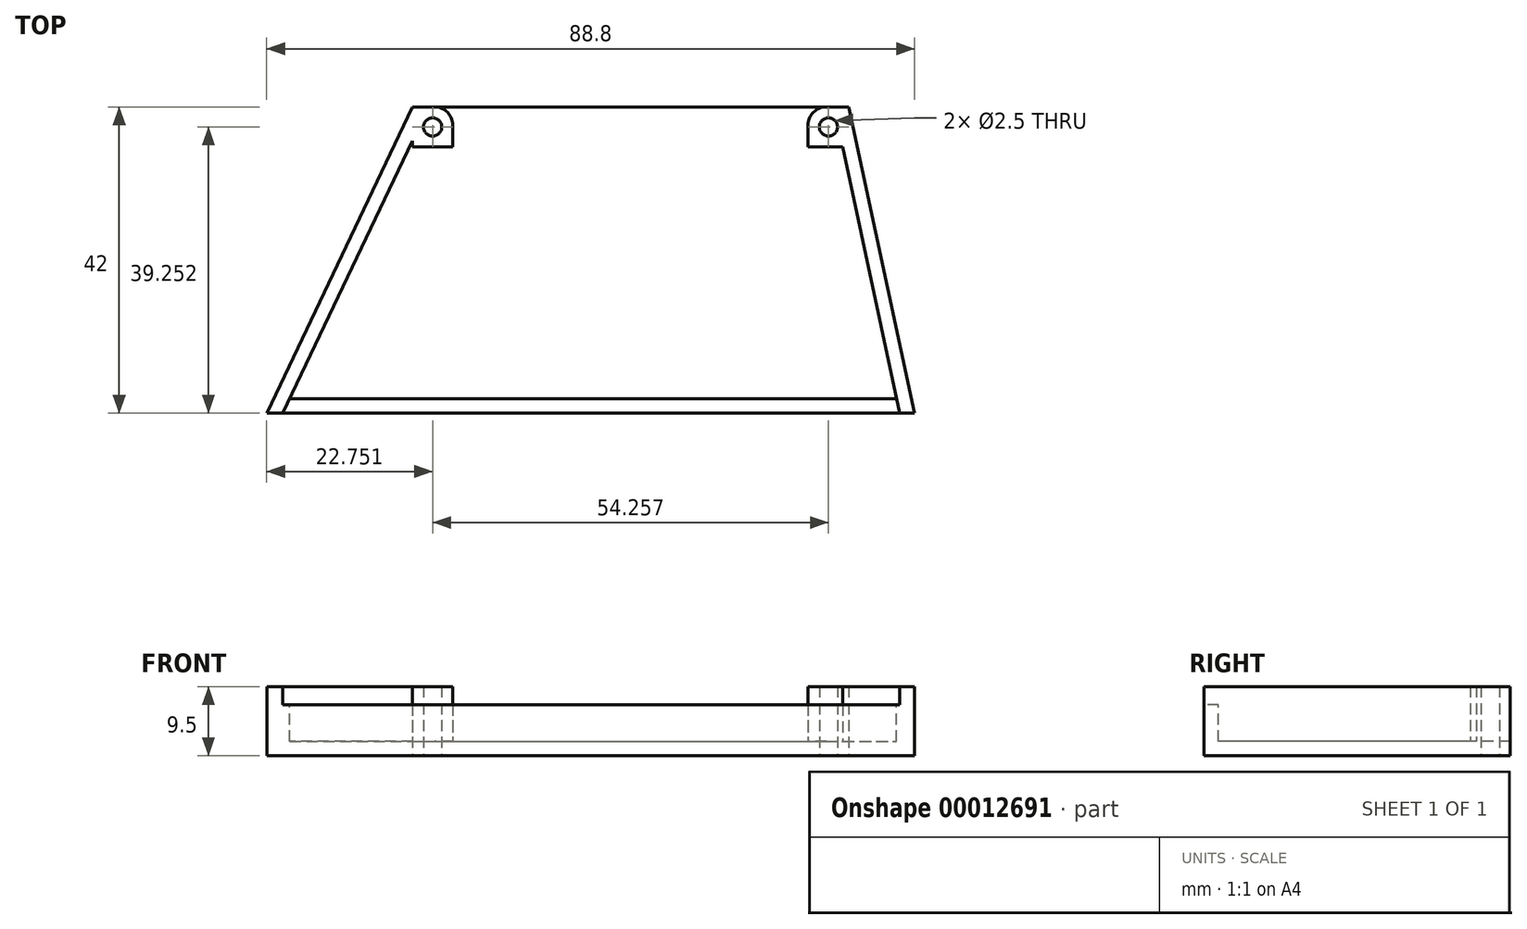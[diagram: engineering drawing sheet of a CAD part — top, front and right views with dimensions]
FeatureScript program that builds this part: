
annotation { "Feature Type Name" : "Feature", "Feature Type Description" : "" }
export const myFeature = defineFeature(function(context is Context, id is Id, definition is map)
    precondition{}
    {
        {
            var Q0;
            Q0=qCreatedBy(makeId("Top.planeOp"),FACE);
            var sketch = newSketch(context, id + "F0", { "sketchPlane" : qUnion([Q0])});
            skLineSegment(sketch, "E0", {"start": v(-30.55, 19.42) * mm, "end": v(29.25, 19.42) * mm});
            skLineSegment(sketch, "E1", {"start": v(-50.55, -22.58) * mm, "end": v(38.25, -22.58) * mm});
            skLineSegment(sketch, "E2", {"start": v(29.25, 19.42) * mm, "end": v(38.25, -22.58) * mm});
            skLineSegment(sketch, "E3", {"start": v(-30.55, 19.42) * mm, "end": v(-50.55, -22.58) * mm});
            skSolve(sketch);
        }
        {
            var Q0;
            Q0 = qSketchRegion(id + "F0", true);
            extrude(context, id + "F1", {"entities" : qUnion([Q0]), "depth" : 2 * mm});
        }
        {
            var Q0;
            Q0=makeQuery(id+"F1.opExtrude","CAP_FACE",FACE,{"disambiguationData":[OSD([sQuery(id+"F0.wireOp",EDGE,"E0"),sQuery(id+"F0.wireOp",EDGE,"E1"),sQuery(id+"F0.wireOp",EDGE,"E2"),sQuery(id+"F0.wireOp",EDGE,"E3")])],"isStart":false});
            var sketch = newSketch(context, id + "F2", { "sketchPlane" : qUnion([Q0])});
            skPoint(sketch, "E4.rect.middle", {"position": v(26.46, 16.67) * mm});
            skLineSegment(sketch, "E4.rect.right", {"start": v(29.25, 19.42) * mm, "end": v(29.25, 13.92) * mm});
            skLineSegment(sketch, "E4.rect.top", {"start": v(23.66, 13.92) * mm, "end": v(29.25, 13.92) * mm});
            skLineSegment(sketch, "E4.rect.bottom", {"start": v(26.16, 19.42) * mm, "end": v(29.25, 19.42) * mm});
            skCircle(sketch, "E5", {"center": v(26.46, 16.67) * mm, "radius": 1.25 * mm});
            skLineSegment(sketch, "E4.rect.left", {"start": v(23.66, 16.92) * mm, "end": v(23.66, 13.92) * mm});
            skPoint(sketch, "E6.visualSharp", {"position": v(23.66, 19.42) * mm});
            skArc(sketch, "E6.filletArc", {"start": v(26.16, 19.42) * mm, "mid": v(24.4, 18.7) * mm, "end": v(23.66, 16.92) * mm});
            skLineSegment(sketch, "E7", {"start": v(29.25, 19.42) * mm, "end": v(38.25, -22.58) * mm});
            skLineSegment(sketch, "E8.0", {"start": v(28.38, 13.92) * mm, "end": v(36.2, -22.58) * mm});
            skLineSegment(sketch, "E9", {"start": v(38.25, -22.58) * mm, "end": v(36.2, -22.58) * mm});
            skLineSegment(sketch, "E10.top", {"start": v(-30.55, 13.92) * mm, "end": v(-25.05, 13.92) * mm});
            skLineSegment(sketch, "E10.left", {"start": v(-30.55, 19.42) * mm, "end": v(-30.55, 13.92) * mm});
            skLineSegment(sketch, "E10.right", {"start": v(-25.05, 16.92) * mm, "end": v(-25.05, 13.92) * mm});
            skLineSegment(sketch, "E11", {"start": v(-30.55, 19.42) * mm, "end": v(-27.55, 19.42) * mm});
            skLineSegment(sketch, "E12", {"start": v(-30.55, 19.42) * mm, "end": v(-50.55, -22.58) * mm});
            skLineSegment(sketch, "E13.0", {"start": v(-30.55, 14.77) * mm, "end": v(-48.33, -22.58) * mm});
            skLineSegment(sketch, "E14", {"start": v(-50.55, -22.58) * mm, "end": v(-48.33, -22.58) * mm});
            skArc(sketch, "E15.filletArc", {"start": v(-25.05, 16.92) * mm, "mid": v(-25.78, 18.7) * mm, "end": v(-27.55, 19.42) * mm});
            skCircle(sketch, "E16", {"center": v(-27.8, 16.67) * mm, "radius": 1.25 * mm});
            skSolve(sketch);
        }
        {
            var Q0;
            Q0 = qSketchRegion(id + "F2", true);
            extrude(context, id + "F3", {"entities" : qUnion([Q0]), "operationType" : NewBodyOperationType.ADD, "depth" : 7.5 * mm});
        }
        {
            var Q0;
            Q0=sQuery(id+"F2.wireOp",VERTEX,"E16.center");
            var Q1;
            Q1=sQuery(id+"F2.wireOp",VERTEX,"E4.rect.middle");
            var Q2;
            Q2=makeQuery(id+"F1.opExtrude","SWEPT_BODY",BODY,{"disambiguationData":[OSD([sQuery(id+"F0.wireOp",EDGE,"E0"),sQuery(id+"F0.wireOp",EDGE,"E1"),sQuery(id+"F0.wireOp",EDGE,"E2"),sQuery(id+"F0.wireOp",EDGE,"E3")])]});
            hole(context, id + "F4", {"style" : HoleStyle.SIMPLE, "holeDiameter" : 2.5 * mm, "endStyle" : HoleEndStyle.THROUGH, "locations" : qUnion([Q0, Q1]), "scope" : qUnion([Q2])});
        }
        {
            var Q0;
            {var subQ8=sQuery(id+"F2.wireOp",EDGE,"E4.rect.left");Q0=makeQuery(id+"F2.imprint","IMPRINT",FACE,{"disambiguationData":[TD([[makeQuery(id+"F2.imprint","IMPRINT",EDGE,{"derivedFrom":subQ8}),-1.0]])]});}
            var sketch = newSketch(context, id + "F5", { "sketchPlane" : qUnion([Q0])});
            skLineSegment(sketch, "E17.0", {"start": v(-50.55, -22.58) * mm, "end": v(-48.33, -22.58) * mm});
            skLineSegment(sketch, "E18.0", {"start": v(38.25, -22.58) * mm, "end": v(36.2, -22.58) * mm});
            skLineSegment(sketch, "E19", {"start": v(-48.33, -22.58) * mm, "end": v(36.2, -22.58) * mm});
            skLineSegment(sketch, "E20.0", {"start": v(-48.33, -20.58) * mm, "end": v(36.2, -20.58) * mm});
            skLineSegment(sketch, "E21", {"start": v(-48.33, -20.58) * mm, "end": v(-48.33, -22.58) * mm});
            skLineSegment(sketch, "E22", {"start": v(36.2, -20.58) * mm, "end": v(36.2, -22.58) * mm});
            skSolve(sketch);
        }
        {
            var Q0;
            Q0 = qSketchRegion(id + "F5", true);
            extrude(context, id + "F6", {"entities" : qUnion([Q0]), "operationType" : NewBodyOperationType.ADD, "depth" : 5 * mm});
        }
    });
